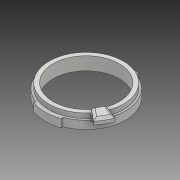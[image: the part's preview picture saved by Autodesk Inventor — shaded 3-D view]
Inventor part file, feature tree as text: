
AUTODESK INVENTOR PART (.ipt)
format: ipt  version: 2018 (Build 220112000, 112)  size: 303,104 bytes
history: native  units: mm
features: extrude x4, sketch x4, chamfer x2, other x1, mirror x1
ambient origin geometry x8: Origin, YZ Plane, XZ Plane, XY Plane, X Axis, Y Axis, Z Axis, Center Point
bodies: Body1 (feature_tree)
feature tree (12):
  other  "ソリッド1"
  extrude  "押し出し1"  Depth=5.0mm
  extrude  "押し出し2"  Depth=40.5mm
  mirror  "ミラー1"
  extrude  "押し出し7"  Depth=8.0mm TaperAngle=0.0deg
  chamfer  "面取り4"  Distance=1.2mm
  extrude  "押し出し8"  Depth=24.43461mm
  chamfer  "面取り5"  Distance=5.0mm
  sketch  "スケッチ1"
  sketch  "スケッチ2"
  sketch  "スケッチ4"
  sketch  "スケッチ7"
